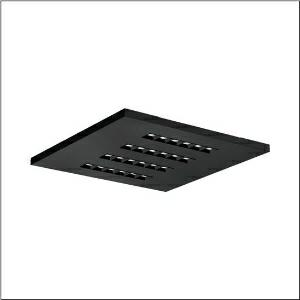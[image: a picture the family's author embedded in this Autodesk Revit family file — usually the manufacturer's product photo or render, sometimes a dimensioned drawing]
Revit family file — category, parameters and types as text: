
# Revit family: silica_r__21_square_51mx6kdu34b_186d
name_source: partatom
category: Lighting Fixtures
units: mm (PartAtom-declared; Revit-internal decimal feet)

## family parameters
Cut with Voids When Loaded = No
Host = Face
Light Source = No
Part Type = Normal
Room Calculation Point = No
Round Connector Dimension = Use Diameter
Shared = No

## types (1)
- --- (1 x LED, 4600 lm, 31.9 W, 3000K)
    Apparent Load = 32 VA
    CIE Flux Codes = 86 100 100 100 100
    Color Rendering = 80
    Color Temperature = 3000K
    Default Elevation = 1800 mm
    Description = Silica® 21 Square, office luminaire, primary light control with lens, of PMMA, primary anti-glare with reflector, of PC, black, CAT 2 (L<= 3000cd/m²), light emission: direct distribution, primary light characteristic: symmetric, installation type: lay-in mounting, LED, rated luminous flux: 4.600lm, luminous efficacy: 144lm/W, light colour: 830, colour temperature: 3000K, control gear: DALI 2, with terminal, 5-pole, mains connection: 220..240V, AC, 50/60Hz, rated input power: 31.9W, luminaire housing, of aluminium, matt jet black (RAL 9005), module: M625, length: 622mm, width: 622mm, height: 33mm, protection rating (complete): IP20, insulation class (complete): insulation class I (protective earthing), certification: CE, ENEC, VDE, permissible operating ambient temperature: -20..+40°C, standard: EN 50419, packaging unit: 1 piece
    Height = 0 mm  [stored 0 ft]
    Lamp = 1 x LED
    Lamp Light Flux = 4600 lm
    Lamp Power = 31.9 W
    Lamp count = 1
    Length = 622 mm
    Luminous efficacy = 144 lm/W
    Manufacturer = Siteco
    ModVariant = No
    Model = 51MX6KDU34B
    Mounting Place = Ceiling
    Mounting Type = Recessed
    Number of Poles = 1
    OnlyDefault = Yes
    Power Factor = 1
    Product Name = Silica® 21 Square
    Product group = office luminaire | ceiling recessed
    ProductGroupID = 401
    Protection Class = Protection class I
    Protection Degree = IP 20
    RLX_Detail_Level = 1
    RLX_Emergency_Light_Flux = 0 lm
    RLX_Emergency_Type = 0
    RLX_Emergency_Type_DB = No
    RlxData = <blob elided: 24985 chars, md5=b2907595>
    Socket = socket
    Standby Power = 0 W
    System Light Flux = 4600 lm
    System Power = 32 W
    Type Comments = factory setting: luminous flux: 100 % | dim-lin: 254 | 430 mA
    Type Image = l_1275204.jpg
    URL = http://relux.com
    VarID = @adj_083908
    Voltage = 0 V
    Weight = 0.00 kg
    Width = 622 mm

note: [stored X ft] marks values corroborated as IEEE doubles in the binary element streams (Revit-internal decimal feet)

## geometry (parser evidence)
native form markers: Blend x4, Sweep x13
no freeform markers — native parametric forms only
